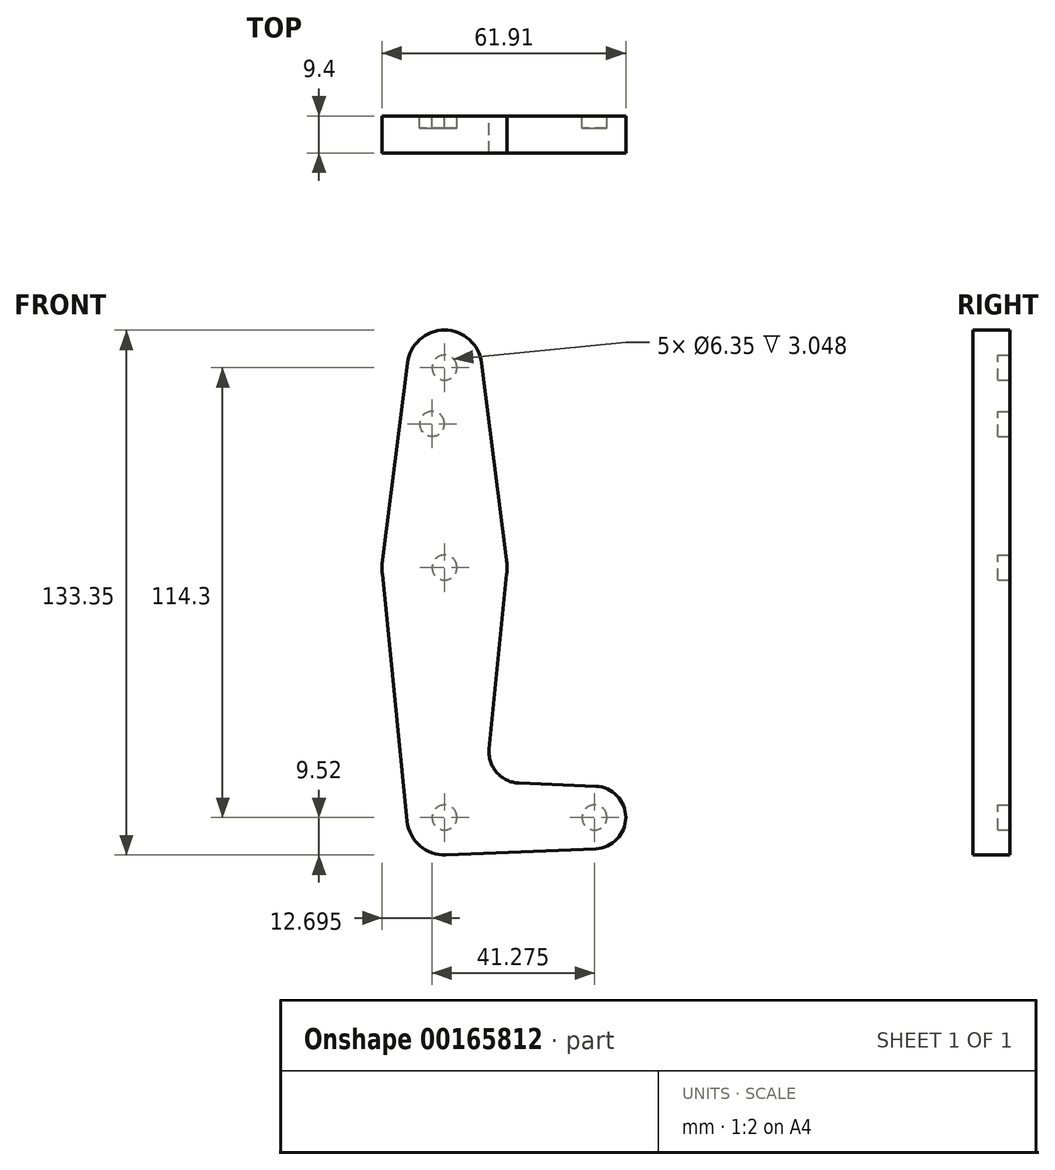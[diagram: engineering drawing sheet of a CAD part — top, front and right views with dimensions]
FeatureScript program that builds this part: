
annotation { "Feature Type Name" : "Feature", "Feature Type Description" : "" }
export const myFeature = defineFeature(function(context is Context, id is Id, definition is map)
    precondition{}
    {
        {
            var Q0;
            Q0=qCreatedBy(makeId("Front.planeOp"),FACE);
            var sketch = newSketch(context, id + "F0", { "sketchPlane" : qUnion([Q0])});
            skLineSegment(sketch, "E0", {"start": v(0, 0) * mm, "end": v(0, 114.3) * mm, "construction": true});
            skLineSegment(sketch, "E1", {"start": v(0, 0) * mm, "end": v(38.1, 0) * mm, "construction": true});
            skCircle(sketch, "E2", {"center": v(0, 114.3) * mm, "radius": 9.52 * mm});
            skCircle(sketch, "E3", {"center": v(0, 0) * mm, "radius": 9.53 * mm});
            skCircle(sketch, "E4", {"center": v(38.1, 0) * mm, "radius": 7.94 * mm});
            skCircle(sketch, "E5", {"center": v(0, 63.5) * mm, "radius": 15.88 * mm});
            skLineSegment(sketch, "E6", {"start": v(-9.45, 115.5) * mm, "end": v(-15.75, 65.48) * mm});
            skLineSegment(sketch, "E7", {"start": v(9.45, 115.5) * mm, "end": v(15.75, 65.48) * mm});
            skLineSegment(sketch, "E8", {"start": v(38.43, 7.93) * mm, "end": v(18.9, 8.74) * mm});
            skLineSegment(sketch, "E9", {"start": v(38.43, -7.93) * mm, "end": v(0.4, -9.52) * mm});
            skLineSegment(sketch, "E10", {"start": v(-9.48, -0.95) * mm, "end": v(-15.8, 61.91) * mm});
            skLineSegment(sketch, "E11", {"start": v(11.33, 17.48) * mm, "end": v(15.8, 61.91) * mm});
            skCircle(sketch, "E12", {"center": v(0, 114.3) * mm, "radius": 3.18 * mm});
            skCircle(sketch, "E13", {"center": v(0, 63.5) * mm, "radius": 3.18 * mm});
            skCircle(sketch, "E14", {"center": v(0, 0) * mm, "radius": 3.18 * mm});
            skCircle(sketch, "E15", {"center": v(38.1, 0) * mm, "radius": 3.18 * mm});
            skCircle(sketch, "E16", {"center": v(-3.17, 100.03) * mm, "radius": 3.18 * mm});
            skPoint(sketch, "E17.newPointA", {"position": v(0, 9.53) * mm});
            skArc(sketch, "E17.filletArc", {"start": v(11.33, 17.48) * mm, "mid": v(13.23, 11.48) * mm, "end": v(18.9, 8.74) * mm});
            skSolve(sketch);
        }
        {
            var Q0;
            Q0 = qSketchRegion(id + "F0", true);
            extrude(context, id + "F1", {"entities" : qUnion([Q0]), "depth" : 3.05 * mm});
        }
        {
            var Q0;
            Q0=makeQuery(id+"F1.opExtrude","CAP_FACE",FACE,{"disambiguationData":[OSD([sQuery(id+"F0.wireOp",EDGE,"E2"),sQuery(id+"F0.wireOp",EDGE,"E3"),sQuery(id+"F0.wireOp",EDGE,"E4"),sQuery(id+"F0.wireOp",EDGE,"E5"),sQuery(id+"F0.wireOp",EDGE,"E6"),sQuery(id+"F0.wireOp",EDGE,"E7"),sQuery(id+"F0.wireOp",EDGE,"E8"),sQuery(id+"F0.wireOp",EDGE,"E9"),sQuery(id+"F0.wireOp",EDGE,"E10"),sQuery(id+"F0.wireOp",EDGE,"E11"),sQuery(id+"F0.wireOp",EDGE,"E12"),sQuery(id+"F0.wireOp",EDGE,"E13"),sQuery(id+"F0.wireOp",EDGE,"E14"),sQuery(id+"F0.wireOp",EDGE,"E15"),sQuery(id+"F0.wireOp",EDGE,"E16"),sQuery(id+"F0.wireOp",EDGE,"E17.filletArc")])],"isStart":false});
            var sketch = newSketch(context, id + "F2", { "sketchPlane" : qUnion([Q0])});
            skArc(sketch, "E18.0.0", {"start": v(9.45, 115.5) * mm, "mid": v(0, 123.83) * mm, "end": v(-9.45, 115.5) * mm});
            skLineSegment(sketch, "E18.0.1", {"start": v(-9.45, 115.5) * mm, "end": v(-15.75, 65.48) * mm});
            skArc(sketch, "E18.0.2", {"start": v(-15.75, 65.48) * mm, "mid": v(-15.87, 63.7) * mm, "end": v(-15.8, 61.91) * mm});
            skLineSegment(sketch, "E18.0.3", {"start": v(-15.8, 61.91) * mm, "end": v(-9.48, -0.95) * mm});
            skArc(sketch, "E18.0.4", {"start": v(-9.48, -0.95) * mm, "mid": v(-6.24, -7.2) * mm, "end": v(0.4, -9.52) * mm});
            skLineSegment(sketch, "E18.0.5", {"start": v(0.4, -9.52) * mm, "end": v(38.43, -7.93) * mm});
            skArc(sketch, "E18.0.6", {"start": v(38.43, -7.93) * mm, "mid": v(46.04, 0) * mm, "end": v(38.43, 7.93) * mm});
            skLineSegment(sketch, "E18.0.7", {"start": v(38.43, 7.93) * mm, "end": v(18.9, 8.74) * mm});
            skArc(sketch, "E18.0.8", {"start": v(18.9, 8.74) * mm, "mid": v(13.23, 11.48) * mm, "end": v(11.33, 17.48) * mm});
            skLineSegment(sketch, "E18.0.9", {"start": v(11.33, 17.48) * mm, "end": v(15.8, 61.91) * mm});
            skArc(sketch, "E18.0.10", {"start": v(15.8, 61.91) * mm, "mid": v(15.87, 63.7) * mm, "end": v(15.75, 65.48) * mm});
            skLineSegment(sketch, "E18.0.11", {"start": v(15.75, 65.48) * mm, "end": v(9.45, 115.5) * mm});
            skSolve(sketch);
        }
        {
            var Q0;
            Q0 = qSketchRegion(id + "F2", true);
            extrude(context, id + "F3", {"entities" : qUnion([Q0]), "operationType" : NewBodyOperationType.ADD, "depth" : 6.35 * mm});
        }
    });
